# Revit family: Vandal_Resistant_Hook_Strip-Bobrick-B-985
name_source: partatom
category: Specialty Equipment
revit_build: Autodesk Revit 2014 (Build: 20130308_1515(x64)
units: mm (PartAtom-declared; Revit-internal decimal feet)

## types (1)
- B-958
    Assembly Code = C1030200
    Default Elevation = 40"
    Description = Vandal-Resistant Clothes Hook Strip (Secured From Front)
    Finish = Metal-Bobrick-Type-304-Heavy Gauge Steel
    Height = 5 1/2"
    Installation Type = Wall-Mounted
    Length = 18"
    Manufacturer = Bobrick
    Material = Metal-Bobrick-Type-304-Heavy Gauge Steel
    Model = B-958
    Price = Prices may vary. Please consult Manufacturer Representative for most up-to-date price list.
    Product Documentation Link = http://www.bobrick.com
    Product Page URL = http://www.bobrick.com
    URL = http://www.bobrick.com
    Warranty Information = 1 Year Limited Warranty
    Width = 2 1/8"

## geometry (parser evidence)
native form markers: Sweep x1
no freeform markers — native parametric forms only
